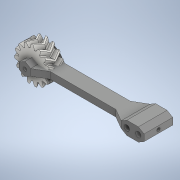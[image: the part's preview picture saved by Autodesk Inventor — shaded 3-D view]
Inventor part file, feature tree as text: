
AUTODESK INVENTOR PART (.ipt)
format: ipt  version: 2020 (Build 240168000, 168)  size: 985,088 bytes
history: native  units: in
note: dims shown in document units (in); Inventor stores cm internally (conversion verified against a paired STEP export)
features: sketch x5, extrude x4, other x3, plane x2, mirror x1, projected_geometry x1
ambient origin geometry x8: Origin, YZ Plane, XZ Plane, XY Plane, X Axis, Y Axis, Z Axis, Center Point
bodies: Solid1 (feature_tree), Solid2 (feature_tree)
feature tree (16):
  other  "Spur Gear1"
  plane  "Work Plane3"
  extrude  "Extrusion1"  Depth=3.4256in
  plane  "Work Plane1"
  extrude  "Extrusion2"  Depth=0.7874in
  sketch  "Sketch4"  dims[d4=0.0in d5=0.0906in]
  extrude  "Extrusion4"  Depth=0.0906in
  mirror  "Mirror3"
  extrude  "Extrusion11"  Depth=0.315in
  sketch  "Sketch1"  dims[d0=0.1818in d1=3.4256in]
  sketch  "Sketch2"  dims[d2=0.0945in d3=0.7874in]
  sketch  "Sketch5"  dims[d6=0.7874in d7=0.0in d29=0.315in]
  other  "Solid1::Spur Gear1"
  other  "TaggingFeature1"
  projected_geometry  "Projected Loop11"
  sketch  "Sketch15"  dims[d31=0.315in d33=0.1476in d34=0.2362in d35=0.0in d38=0.315in d69=2.4807in d70=0.3937in d71=0.1969in d79=0.0in d80=0.3937in d81=0.0in]
